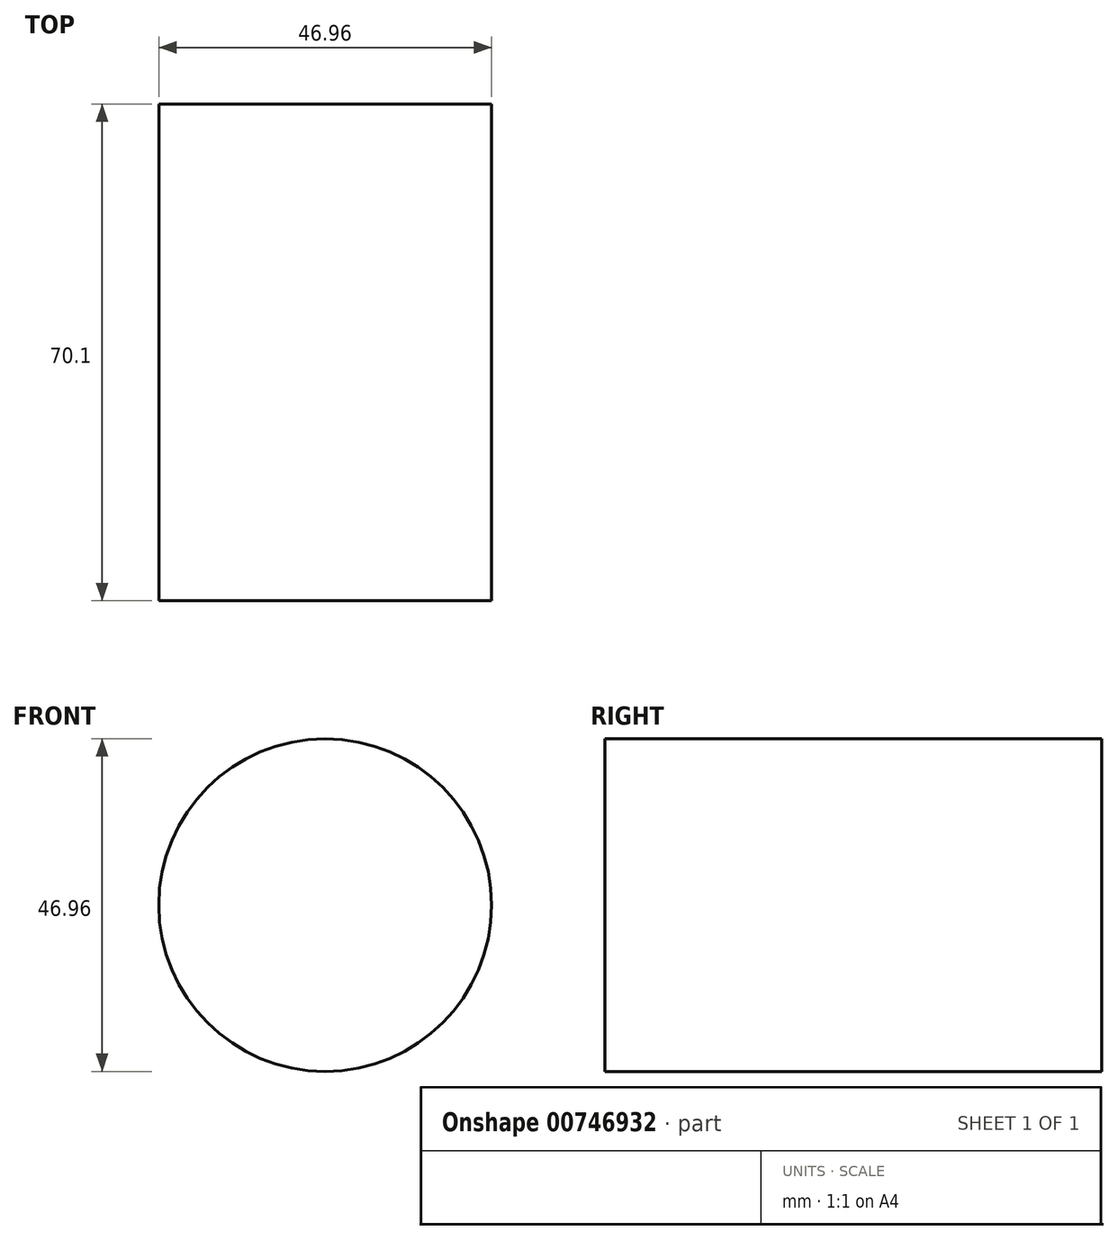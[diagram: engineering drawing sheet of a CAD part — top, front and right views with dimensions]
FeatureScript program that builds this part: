
annotation { "Feature Type Name" : "Feature", "Feature Type Description" : "" }
export const myFeature = defineFeature(function(context is Context, id is Id, definition is map)
    precondition{}
    {
        {
            var Q0;
            Q0=qCreatedBy(makeId("Front.planeOp"),FACE);
            var sketch = newSketch(context, id + "F0", { "sketchPlane" : qUnion([Q0])});
            skCircle(sketch, "E0", {"center": v(0, 23.99) * mm, "radius": 23.48 * mm});
            skSolve(sketch);
        }
        {
            var Q0;
            Q0=makeQuery(id+"F0.imprint","IMPRINT",FACE,{"disambiguationData":[TD([[makeQuery(id+"F0.imprint","IMPRINT",EDGE,{"derivedFrom":sQuery(id+"F0.wireOp",EDGE,"E0")}),1.0]])]});
            extrude(context, id + "F1", {"entities" : qUnion([Q0]), "depth" : 70.1 * mm, "offsetDistance" : 25.4 * mm});
        }
    });
